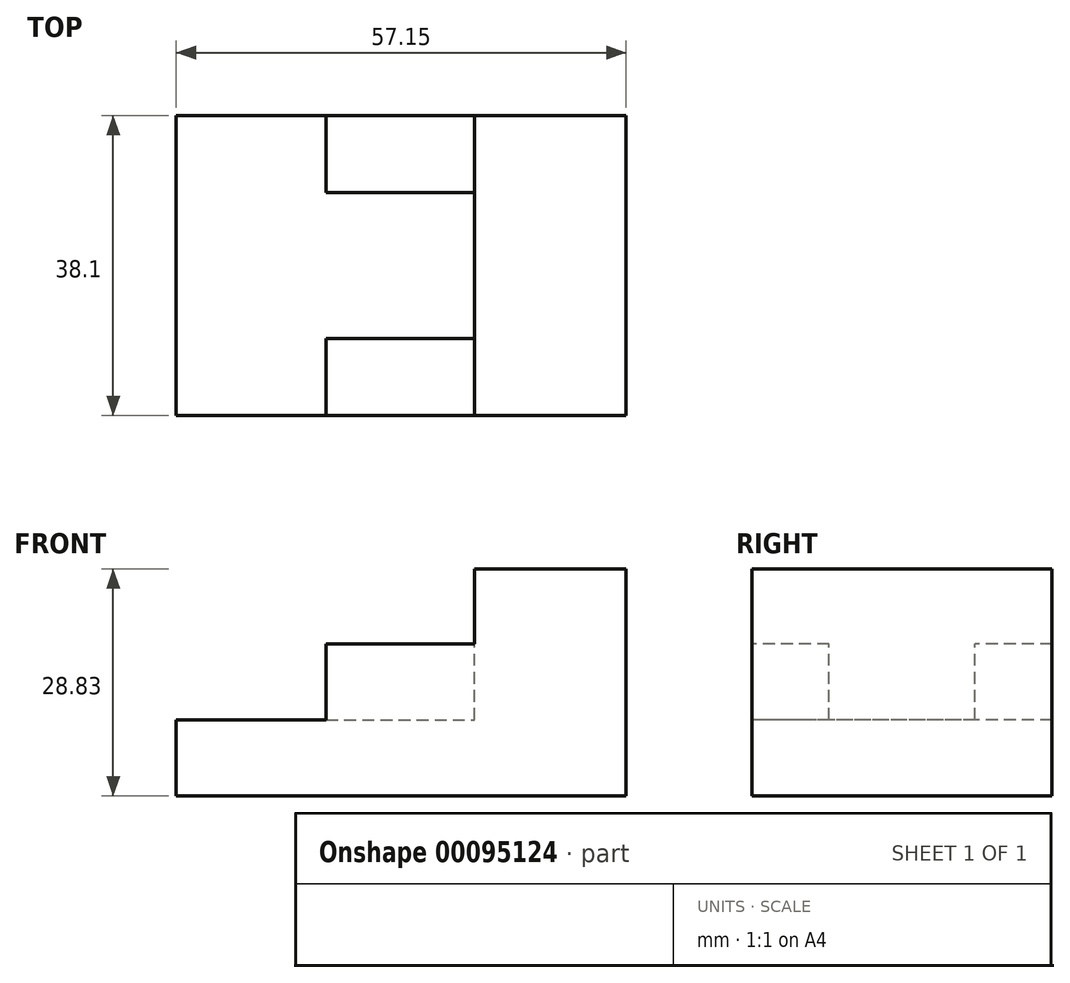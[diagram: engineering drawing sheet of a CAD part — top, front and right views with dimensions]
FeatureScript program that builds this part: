
annotation { "Feature Type Name" : "Feature", "Feature Type Description" : "" }
export const myFeature = defineFeature(function(context is Context, id is Id, definition is map)
    precondition{}
    {
        {
            var Q0;
            Q0=qCreatedBy(makeId("Top.planeOp"),FACE);
            var sketch = newSketch(context, id + "F0", { "sketchPlane" : qUnion([Q0])});
            skLineSegment(sketch, "E0.bottom", {"start": v(0, 18.22) * mm, "end": v(-57.15, 18.22) * mm});
            skLineSegment(sketch, "E0.top", {"start": v(0, -19.88) * mm, "end": v(-57.15, -19.88) * mm});
            skLineSegment(sketch, "E0.left", {"start": v(0, 18.22) * mm, "end": v(0, -19.88) * mm});
            skLineSegment(sketch, "E0.right", {"start": v(-57.15, 18.22) * mm, "end": v(-57.15, -19.88) * mm});
            skSolve(sketch);
        }
        {
            var Q0;
            Q0 = qSketchRegion(id + "F0", true);
            extrude(context, id + "F1", {"entities" : qUnion([Q0]), "depth" : 28.83 * mm});
        }
        {
            var Q0;
            Q0=makeQuery(id+"F1.opExtrude","SWEPT_FACE",FACE,{"disambiguationData":[OSD([sQuery(id+"F0.wireOp",EDGE,"E0.top")])]});
            var sketch = newSketch(context, id + "F2", { "sketchPlane" : qUnion([Q0])});
            skLineSegment(sketch, "E1.bottom", {"start": v(-57.15, 9.65) * mm, "end": v(-38.1, 9.65) * mm});
            skLineSegment(sketch, "E1.top", {"start": v(-57.15, 28.83) * mm, "end": v(-38.1, 28.83) * mm});
            skLineSegment(sketch, "E1.left", {"start": v(-57.15, 9.65) * mm, "end": v(-57.15, 28.83) * mm});
            skLineSegment(sketch, "E1.right", {"start": v(-38.1, 9.65) * mm, "end": v(-38.1, 28.83) * mm});
            skLineSegment(sketch, "E2.bottom", {"start": v(-19.25, 28.83) * mm, "end": v(-38.1, 28.83) * mm});
            skLineSegment(sketch, "E2.left", {"start": v(-19.25, 28.83) * mm, "end": v(-19.25, 19.3) * mm});
            skLineSegment(sketch, "E2.right", {"start": v(-38.1, 28.83) * mm, "end": v(-38.1, 19.24) * mm});
            skLineSegment(sketch, "E3", {"start": v(-19.25, 19.3) * mm, "end": v(-38.1, 19.3) * mm});
            skSolve(sketch);
        }
        {
            var Q0;
            Q0 = qSketchRegion(id + "F2", true);
            extrude(context, id + "F3", {"entities" : qUnion([Q0]), "operationType" : NewBodyOperationType.REMOVE, "endBound" : BoundingType.THROUGH_ALL, "oppositeDirection" : true, "depth" : 25.4 * mm});
        }
        {
            var Q0;
            Q0=makeQuery(id+"F3.boolean.opBoolean","COPY",FACE,{"derivedFrom":makeQuery(id+"F3.opExtrude","SWEPT_FACE",FACE,{"disambiguationData":[OSD([sQuery(id+"F2.wireOp",EDGE,"E3")])]})});
            var sketch = newSketch(context, id + "F4", { "sketchPlane" : qUnion([Q0])});
            skLineSegment(sketch, "E4.bottom", {"start": v(-38.1, 8.44) * mm, "end": v(-19.25, 8.44) * mm});
            skLineSegment(sketch, "E4.top", {"start": v(-38.1, -10.1) * mm, "end": v(-19.25, -10.1) * mm});
            skLineSegment(sketch, "E4.left", {"start": v(-38.1, 8.44) * mm, "end": v(-38.1, -10.1) * mm});
            skLineSegment(sketch, "E4.right", {"start": v(-19.25, 8.44) * mm, "end": v(-19.25, -10.1) * mm});
            skSolve(sketch);
        }
        {
            var Q0;
            Q0 = qSketchRegion(id + "F4", true);
            extrude(context, id + "F5", {"entities" : qUnion([Q0]), "operationType" : NewBodyOperationType.REMOVE, "oppositeDirection" : true, "depth" : 9.65 * mm});
        }
    });
